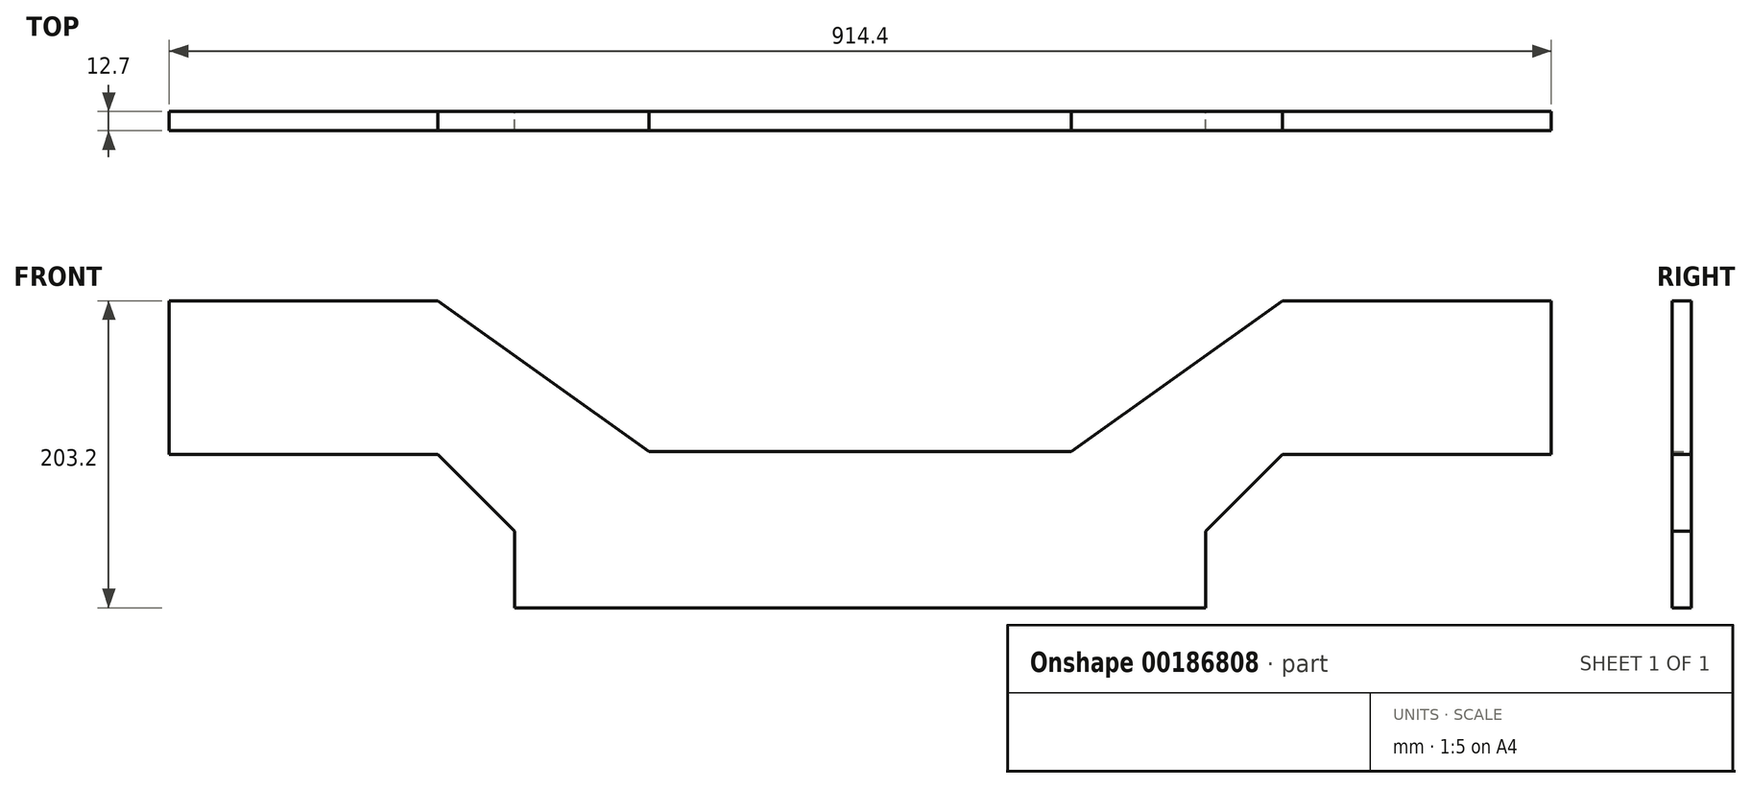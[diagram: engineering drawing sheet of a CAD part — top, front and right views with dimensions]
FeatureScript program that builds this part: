
annotation { "Feature Type Name" : "Feature", "Feature Type Description" : "" }
export const myFeature = defineFeature(function(context is Context, id is Id, definition is map)
    precondition{}
    {
        {
            var Q0;
            Q0=qCreatedBy(makeId("Front.planeOp"),FACE);
            var sketch = newSketch(context, id + "F0", { "sketchPlane" : qUnion([Q0])});
            skLineSegment(sketch, "E0", {"start": v(-228.6, 101.6) * mm, "end": v(-279.4, 152.4) * mm});
            skLineSegment(sketch, "E1", {"start": v(-279.4, 152.4) * mm, "end": v(-457.2, 152.4) * mm});
            skLineSegment(sketch, "E2", {"start": v(-457.2, 152.4) * mm, "end": v(-457.2, 254) * mm});
            skLineSegment(sketch, "E3", {"start": v(-457.2, 254) * mm, "end": v(-279.4, 254) * mm});
            skLineSegment(sketch, "E4", {"start": v(-279.4, 254) * mm, "end": v(-139.7, 154.07) * mm});
            skLineSegment(sketch, "E5", {"start": v(-139.7, 154.07) * mm, "end": v(0, 154.07) * mm});
            skLineSegment(sketch, "E6.MirrorCS", {"start": v(139.7, 154.07) * mm, "end": v(0, 154.07) * mm});
            skLineSegment(sketch, "E7.MirrorCS", {"start": v(279.4, 254) * mm, "end": v(139.7, 154.07) * mm});
            skLineSegment(sketch, "E8.MirrorCS", {"start": v(228.6, 101.6) * mm, "end": v(279.4, 152.4) * mm});
            skLineSegment(sketch, "E9.MirrorCS", {"start": v(457.2, 152.4) * mm, "end": v(457.2, 254) * mm});
            skLineSegment(sketch, "E10.MirrorCS", {"start": v(279.4, 152.4) * mm, "end": v(457.2, 152.4) * mm});
            skLineSegment(sketch, "E11.MirrorCS", {"start": v(457.2, 254) * mm, "end": v(279.4, 254) * mm});
            skLineSegment(sketch, "E12", {"start": v(-228.6, 50.8) * mm, "end": v(228.6, 50.8) * mm});
            skLineSegment(sketch, "E13", {"start": v(-228.6, 101.6) * mm, "end": v(-228.6, 50.8) * mm});
            skLineSegment(sketch, "E14", {"start": v(228.6, 50.8) * mm, "end": v(228.6, 101.6) * mm});
            skSolve(sketch);
        }
        {
            var Q0;
            Q0=makeQuery(id+"F0.imprint","IMPRINT",FACE,{"disambiguationData":[TD([[makeQuery(id+"F0.imprint","IMPRINT",EDGE,{"derivedFrom":sQuery(id+"F0.wireOp",EDGE,"E0")}),-1.0]])]});
            extrude(context, id + "F1", {"entities" : qUnion([Q0]), "depth" : 12.7 * mm});
        }
    });
